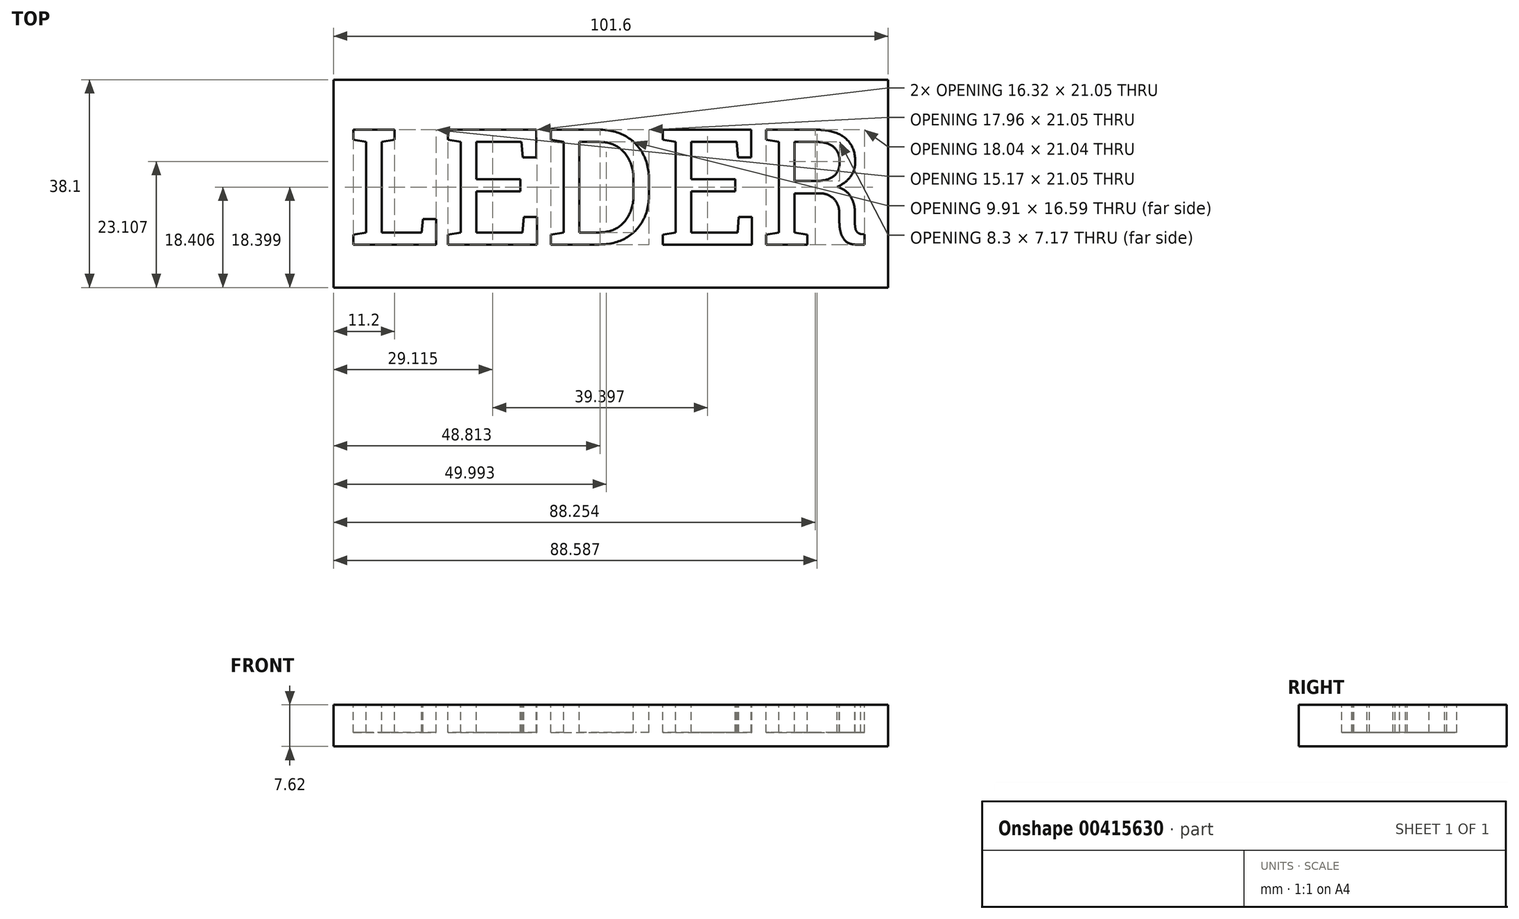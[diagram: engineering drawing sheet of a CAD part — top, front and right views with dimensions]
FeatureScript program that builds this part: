
annotation { "Feature Type Name" : "Feature", "Feature Type Description" : "" }
export const myFeature = defineFeature(function(context is Context, id is Id, definition is map)
    precondition{}
    {
        {
            var Q0;
            Q0=qCreatedBy(makeId("Top.planeOp"),FACE);
            var sketch = newSketch(context, id + "F0", { "sketchPlane" : qUnion([Q0])});
            skLineSegment(sketch, "E0.bottom", {"start": v(50.8, 19.05) * mm, "end": v(-50.8, 19.05) * mm});
            skLineSegment(sketch, "E0.top", {"start": v(50.8, -19.05) * mm, "end": v(-50.8, -19.05) * mm});
            skLineSegment(sketch, "E0.left", {"start": v(50.8, 19.05) * mm, "end": v(50.8, -19.05) * mm});
            skLineSegment(sketch, "E0.right", {"start": v(-50.8, 19.05) * mm, "end": v(-50.8, -19.05) * mm});
            skPoint(sketch, "E0.middle", {"position": v(0, 0) * mm});
            skSolve(sketch);
        }
        {
            var Q0;
            Q0=makeQuery(id+"F0.imprint","IMPRINT",FACE,{"disambiguationData":[TD([[makeQuery(id+"F0.imprint","IMPRINT",EDGE,{"derivedFrom":sQuery(id+"F0.wireOp",EDGE,"E0.bottom")}),1.0]])]});
            extrude(context, id + "F1", {"entities" : qUnion([Q0]), "depth" : 7.62 * mm});
        }
        {
            var Q0;
            Q0=makeQuery(id+"F1.opExtrude","CAP_FACE",FACE,{"disambiguationData":[OSD([sQuery(id+"F0.wireOp",EDGE,"E0.bottom"),sQuery(id+"F0.wireOp",EDGE,"E0.top"),sQuery(id+"F0.wireOp",EDGE,"E0.left"),sQuery(id+"F0.wireOp",EDGE,"E0.right")])],"isStart":false});
            var sketch = newSketch(context, id + "F2", { "sketchPlane" : qUnion([Q0])});
            skLineSegment(sketch, "E1.bottom", {"start": v(50.8, 19.05) * mm, "end": v(-50.8, 19.05) * mm, "construction": true});
            skLineSegment(sketch, "E1.top", {"start": v(50.8, -19.05) * mm, "end": v(-50.8, -19.05) * mm, "construction": true});
            skLineSegment(sketch, "E1.left", {"start": v(50.8, 19.05) * mm, "end": v(50.8, -19.05) * mm, "construction": true});
            skLineSegment(sketch, "E1.right", {"start": v(-50.8, 19.05) * mm, "end": v(-50.8, -19.05) * mm, "construction": true});
            skPoint(sketch, "E1.middle", {"position": v(0, 0) * mm});
            skLineSegment(sketch, "E2", {"start": v(0, 19.05) * mm, "end": v(0, -19.05) * mm, "construction": true});
            skLineSegment(sketch, "E3", {"start": v(0, -19.05) * mm, "end": v(-50.8, 0) * mm, "construction": true});
            skLineSegment(sketch, "E4", {"start": v(-50.8, 0) * mm, "end": v(50.8, 0) * mm, "construction": true});
            skText(sketch, "E5", { "text": "LEDER", "fontName": "RobotoSlab-Regular.ttf"});
            skLineSegment(sketch, "E6", {"start": v(0.05, 10.15) * mm, "end": v(0.05, -11.17) * mm, "construction": true});
            skLineSegment(sketch, "E7", {"start": v(0, 0) * mm, "end": v(0.05, 10.15) * mm, "construction": true});
            const initialGuessF2  = {"E5": [-0.04821, -0.01117, 1, 0, 0.02132]};
            skSetInitialGuess(sketch, initialGuessF2);
            skSolve(sketch);
        }
        {
            var Q0;
            Q0 = qSketchRegion(id + "F2", true);
            extrude(context, id + "F3", {"entities" : qUnion([Q0]), "operationType" : NewBodyOperationType.REMOVE, "oppositeDirection" : true, "depth" : 5.08 * mm});
        }
    });
